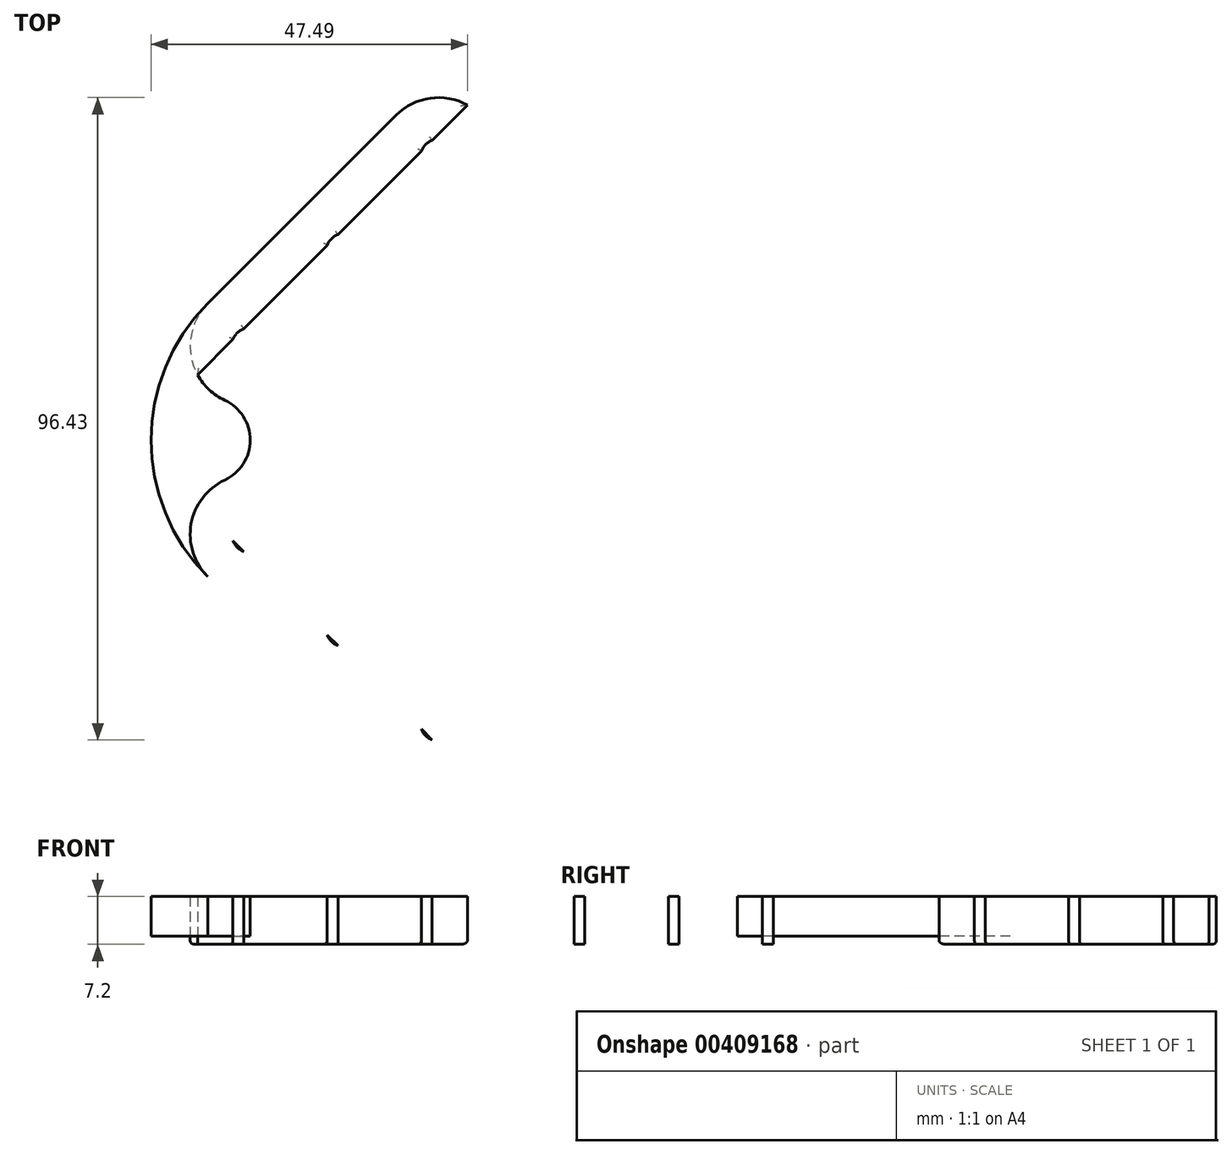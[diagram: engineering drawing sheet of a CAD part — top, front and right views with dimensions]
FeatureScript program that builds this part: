
annotation { "Feature Type Name" : "Feature", "Feature Type Description" : "" }
export const myFeature = defineFeature(function(context is Context, id is Id, definition is map)
    precondition{}
    {
        {
            var Q0;
            Q0=qCreatedBy(makeId("Top.planeOp"),FACE);
            var sketch = newSketch(context, id + "F0", { "sketchPlane" : qUnion([Q0])});
            skLineSegment(sketch, "E0", {"start": v(0, 0) * mm, "end": v(55.95, 55.95) * mm, "construction": true});
            skLineSegment(sketch, "E1", {"start": v(55.95, -55.95) * mm, "end": v(0, 0) * mm, "construction": true});
            skLineSegment(sketch, "E2", {"start": v(0, 14.14) * mm, "end": v(14.14, 0) * mm});
            skLineSegment(sketch, "E3", {"start": v(14.14, 0) * mm, "end": v(0, -14.14) * mm});
            skCircle(sketch, "E4", {"center": v(14.14, 14.14) * mm, "radius": 10 * mm, "construction": true});
            skCircle(sketch, "E5", {"center": v(14.14, 14.14) * mm, "radius": 2.75 * mm});
            skCircle(sketch, "E6", {"center": v(28.28, 28.28) * mm, "radius": 2.75 * mm});
            skCircle(sketch, "E7", {"center": v(42.43, 42.43) * mm, "radius": 2.75 * mm});
            skArc(sketch, "E8", {"start": v(7.78, 20.5) * mm, "mid": v(5.28, 12.58) * mm, "end": v(10.33, 5.99) * mm});
            skArc(sketch, "E9", {"start": v(48.8, 36.06) * mm, "mid": v(48.8, 48.8) * mm, "end": v(36.06, 48.8) * mm});
            skLineSegment(sketch, "E10", {"start": v(7.78, 20.5) * mm, "end": v(36.06, 48.8) * mm});
            skLineSegment(sketch, "E11", {"start": v(23.59, 10.86) * mm, "end": v(20.5, 7.78) * mm, "construction": true});
            skCircle(sketch, "E12.MirrorC", {"center": v(14.14, -14.14) * mm, "radius": 2.75 * mm});
            skLineSegment(sketch, "E13.MirrorCS", {"start": v(0, -14.14) * mm, "end": v(14.14, 0) * mm, "construction": true});
            skCircle(sketch, "E14.MirrorC", {"center": v(28.28, -28.28) * mm, "radius": 2.75 * mm});
            skCircle(sketch, "E15.MirrorC", {"center": v(42.43, -42.43) * mm, "radius": 2.75 * mm});
            skArc(sketch, "E16.MirrorCS", {"start": v(7.78, -20.5) * mm, "mid": v(5.28, -12.58) * mm, "end": v(10.33, -5.99) * mm});
            skLineSegment(sketch, "E17.MirrorCS", {"start": v(0, 0) * mm, "end": v(55.95, -55.95) * mm, "construction": true});
            skCircle(sketch, "E18.MirrorC", {"center": v(14.14, -14.14) * mm, "radius": 10 * mm, "construction": true});
            skArc(sketch, "E19.MirrorCS", {"start": v(48.8, -36.06) * mm, "mid": v(48.8, -48.8) * mm, "end": v(36.06, -48.8) * mm});
            skLineSegment(sketch, "E20.MirrorCS", {"start": v(7.78, -20.5) * mm, "end": v(36.06, -48.8) * mm});
            skArc(sketch, "E21", {"start": v(10.33, 5.99) * mm, "mid": v(14.14, 0) * mm, "end": v(10.33, -5.99) * mm});
            skArc(sketch, "E22", {"start": v(48.8, 36.06) * mm, "mid": v(33.85, 0) * mm, "end": v(48.8, -36.06) * mm});
            skCircle(sketch, "E23", {"center": v(28.28, 28.28) * mm, "radius": 2.5 * mm, "construction": true});
            skLineSegment(sketch, "E24", {"start": v(50.3, 46.77) * mm, "end": v(9.8, 6.26) * mm});
            skLineSegment(sketch, "E25.MirrorCS", {"start": v(46.77, 50.3) * mm, "end": v(6.26, 9.8) * mm});
            skLineSegment(sketch, "E26.MirrorCS", {"start": v(46.77, -50.3) * mm, "end": v(6.26, -9.8) * mm});
            skLineSegment(sketch, "E27.MirrorCS", {"start": v(50.3, -46.77) * mm, "end": v(9.8, -6.26) * mm});
            skArc(sketch, "E28", {"start": v(7.78, 20.5) * mm, "mid": v(-0.72, 0) * mm, "end": v(7.78, -20.5) * mm});
            skSolve(sketch);
        }
        {
            var Q0;
            {var subQ4=sQuery(id+"F0.wireOp",EDGE,"E21");Q0=makeQuery(id+"F0.imprint","IMPRINT",FACE,{"disambiguationData":[TD([[makeQuery(id+"F0.imprint","IMPRINT",EDGE,{"derivedFrom":subQ4}),1.0]])]});}
            var Q1;
            {var subQ0=sQuery(id+"F0.wireOp",EDGE,"E10");Q1=makeQuery(id+"F0.imprint","IMPRINT",FACE,{"disambiguationData":[TD([[makeQuery(id+"F0.imprint","IMPRINT",EDGE,{"derivedFrom":subQ0}),-1.0]])]});}
            var Q2;
            {var subQ0=sQuery(id+"F0.wireOp",EDGE,"E25.MirrorCS");var subQ1=sQuery(id+"F0.wireOp",EDGE,"E6");var subQ2=makeQuery(id+"F0.imprint","INTERSECT",VERTEX,{"disambiguationData":[OD(1.0)],"derivedFrom":[subQ1,subQ0]});Q2=makeQuery(id+"F0.imprint","IMPRINT",FACE,{"disambiguationData":[TD([[makeQuery(id+"F0.imprint","IMPRINT",EDGE,{"disambiguationData":[TD([[subQ2,1.0]])],"derivedFrom":subQ1}),-1.0]])]});}
            var Q3;
            {var subQ0=sQuery(id+"F0.wireOp",EDGE,"E25.MirrorCS");var subQ1=sQuery(id+"F0.wireOp",EDGE,"E7");var subQ2=makeQuery(id+"F0.imprint","INTERSECT",VERTEX,{"disambiguationData":[OD(1.0)],"derivedFrom":[subQ1,subQ0]});Q3=makeQuery(id+"F0.imprint","IMPRINT",FACE,{"disambiguationData":[TD([[makeQuery(id+"F0.imprint","IMPRINT",EDGE,{"disambiguationData":[TD([[subQ2,1.0]])],"derivedFrom":subQ1}),-1.0]])]});}
            var Q4;
            {var subQ0=sQuery(id+"F0.wireOp",EDGE,"E25.MirrorCS");var subQ1=sQuery(id+"F0.wireOp",EDGE,"E5");var subQ2=makeQuery(id+"F0.imprint","INTERSECT",VERTEX,{"disambiguationData":[OD(1.0)],"derivedFrom":[subQ1,subQ0]});Q4=makeQuery(id+"F0.imprint","IMPRINT",FACE,{"disambiguationData":[TD([[makeQuery(id+"F0.imprint","IMPRINT",EDGE,{"disambiguationData":[TD([[subQ2,1.0]])],"derivedFrom":subQ1}),-1.0]])]});}
            var Q5;
            {var subQ0=sQuery(id+"F0.wireOp",EDGE,"E25.MirrorCS");var subQ1=sQuery(id+"F0.wireOp",EDGE,"E5");var subQ2=makeQuery(id+"F0.imprint","INTERSECT",VERTEX,{"disambiguationData":[OD(0.0)],"derivedFrom":[subQ1,subQ0]});Q5=makeQuery(id+"F0.imprint","IMPRINT",FACE,{"disambiguationData":[TD([[makeQuery(id+"F0.imprint","IMPRINT",EDGE,{"disambiguationData":[TD([[subQ2,-1.0]])],"derivedFrom":subQ1}),-1.0]])]});}
            var Q6;
            {var subQ0=sQuery(id+"F0.wireOp",EDGE,"E26.MirrorCS");var subQ1=sQuery(id+"F0.wireOp",EDGE,"E12.MirrorC");var subQ2=makeQuery(id+"F0.imprint","INTERSECT",VERTEX,{"disambiguationData":[OD(0.0)],"derivedFrom":[subQ1,subQ0]});Q6=makeQuery(id+"F0.imprint","IMPRINT",FACE,{"disambiguationData":[TD([[makeQuery(id+"F0.imprint","IMPRINT",EDGE,{"disambiguationData":[TD([[subQ2,-1.0]])],"derivedFrom":subQ1}),1.0]])]});}
            var Q7;
            {var subQ0=sQuery(id+"F0.wireOp",EDGE,"E26.MirrorCS");var subQ1=sQuery(id+"F0.wireOp",EDGE,"E12.MirrorC");var subQ2=makeQuery(id+"F0.imprint","INTERSECT",VERTEX,{"disambiguationData":[OD(1.0)],"derivedFrom":[subQ1,subQ0]});Q7=makeQuery(id+"F0.imprint","IMPRINT",FACE,{"disambiguationData":[TD([[makeQuery(id+"F0.imprint","IMPRINT",EDGE,{"disambiguationData":[TD([[subQ2,1.0]])],"derivedFrom":subQ1}),1.0]])]});}
            var Q8;
            {var subQ0=sQuery(id+"F0.wireOp",EDGE,"E26.MirrorCS");var subQ1=sQuery(id+"F0.wireOp",EDGE,"E14.MirrorC");var subQ2=makeQuery(id+"F0.imprint","INTERSECT",VERTEX,{"disambiguationData":[OD(1.0)],"derivedFrom":[subQ1,subQ0]});Q8=makeQuery(id+"F0.imprint","IMPRINT",FACE,{"disambiguationData":[TD([[makeQuery(id+"F0.imprint","IMPRINT",EDGE,{"disambiguationData":[TD([[subQ2,1.0]])],"derivedFrom":subQ1}),1.0]])]});}
            var Q9;
            {var subQ0=sQuery(id+"F0.wireOp",EDGE,"E26.MirrorCS");var subQ1=sQuery(id+"F0.wireOp",EDGE,"E15.MirrorC");var subQ2=makeQuery(id+"F0.imprint","INTERSECT",VERTEX,{"disambiguationData":[OD(1.0)],"derivedFrom":[subQ1,subQ0]});Q9=makeQuery(id+"F0.imprint","IMPRINT",FACE,{"disambiguationData":[TD([[makeQuery(id+"F0.imprint","IMPRINT",EDGE,{"disambiguationData":[TD([[subQ2,1.0]])],"derivedFrom":subQ1}),1.0]])]});}
            var Q10;
            {var subQ0=sQuery(id+"F0.wireOp",EDGE,"E20.MirrorCS");Q10=makeQuery(id+"F0.imprint","IMPRINT",FACE,{"disambiguationData":[TD([[makeQuery(id+"F0.imprint","IMPRINT",EDGE,{"derivedFrom":subQ0}),1.0]])]});}
            var Q11;
            {var subQ3=sQuery(id+"F0.wireOp",EDGE,"E21");Q11=makeQuery(id+"F0.imprint","IMPRINT",FACE,{"disambiguationData":[TD([[makeQuery(id+"F0.imprint","IMPRINT",EDGE,{"derivedFrom":subQ3}),-1.0]])]});}
            var Q12;
            {var subQ1=sQuery(id+"F0.wireOp",EDGE,"E2");var subQ3=sQuery(id+"F0.wireOp",EDGE,"E28");var subQ4=makeQuery(id+"F0.imprint","INTERSECT",VERTEX,{"derivedFrom":[subQ1,subQ3]});Q12=makeQuery(id+"F0.imprint","IMPRINT",FACE,{"disambiguationData":[TD([[makeQuery(id+"F0.imprint","IMPRINT",EDGE,{"disambiguationData":[TD([[subQ4,-1.0]])],"derivedFrom":subQ3}),1.0]])]});}
            extrude(context, id + "F1", {"entities" : qUnion([Q0, Q1, Q2, Q3, Q4, Q5, Q6, Q7, Q8, Q9, Q10, Q11, Q12]), "depth" : 6 * mm, "offsetDistance" : 25 * mm});
        }
        {
            var Q0;
            {var subQ0=sQuery(id+"F0.wireOp",EDGE,"E25.MirrorCS");var subQ1=sQuery(id+"F0.wireOp",EDGE,"E7");var subQ2=makeQuery(id+"F0.imprint","INTERSECT",VERTEX,{"disambiguationData":[OD(1.0)],"derivedFrom":[subQ1,subQ0]});Q0=makeQuery(id+"F0.imprint","IMPRINT",FACE,{"disambiguationData":[TD([[makeQuery(id+"F0.imprint","IMPRINT",EDGE,{"disambiguationData":[TD([[subQ2,1.0]])],"derivedFrom":subQ1}),-1.0]])]});}
            var Q1;
            {var subQ0=sQuery(id+"F0.wireOp",EDGE,"E25.MirrorCS");var subQ1=sQuery(id+"F0.wireOp",EDGE,"E6");var subQ2=makeQuery(id+"F0.imprint","INTERSECT",VERTEX,{"disambiguationData":[OD(1.0)],"derivedFrom":[subQ1,subQ0]});Q1=makeQuery(id+"F0.imprint","IMPRINT",FACE,{"disambiguationData":[TD([[makeQuery(id+"F0.imprint","IMPRINT",EDGE,{"disambiguationData":[TD([[subQ2,1.0]])],"derivedFrom":subQ1}),-1.0]])]});}
            var Q2;
            {var subQ0=sQuery(id+"F0.wireOp",EDGE,"E25.MirrorCS");var subQ1=sQuery(id+"F0.wireOp",EDGE,"E5");var subQ2=makeQuery(id+"F0.imprint","INTERSECT",VERTEX,{"disambiguationData":[OD(1.0)],"derivedFrom":[subQ1,subQ0]});Q2=makeQuery(id+"F0.imprint","IMPRINT",FACE,{"disambiguationData":[TD([[makeQuery(id+"F0.imprint","IMPRINT",EDGE,{"disambiguationData":[TD([[subQ2,1.0]])],"derivedFrom":subQ1}),-1.0]])]});}
            var Q3;
            {var subQ0=sQuery(id+"F0.wireOp",EDGE,"E25.MirrorCS");var subQ1=sQuery(id+"F0.wireOp",EDGE,"E5");var subQ2=makeQuery(id+"F0.imprint","INTERSECT",VERTEX,{"disambiguationData":[OD(0.0)],"derivedFrom":[subQ1,subQ0]});Q3=makeQuery(id+"F0.imprint","IMPRINT",FACE,{"disambiguationData":[TD([[makeQuery(id+"F0.imprint","IMPRINT",EDGE,{"disambiguationData":[TD([[subQ2,-1.0]])],"derivedFrom":subQ1}),-1.0]])]});}
            var Q4;
            {var subQ0=sQuery(id+"F0.wireOp",EDGE,"E26.MirrorCS");var subQ1=sQuery(id+"F0.wireOp",EDGE,"E12.MirrorC");var subQ2=makeQuery(id+"F0.imprint","INTERSECT",VERTEX,{"disambiguationData":[OD(0.0)],"derivedFrom":[subQ1,subQ0]});Q4=makeQuery(id+"F0.imprint","IMPRINT",FACE,{"disambiguationData":[TD([[makeQuery(id+"F0.imprint","IMPRINT",EDGE,{"disambiguationData":[TD([[subQ2,-1.0]])],"derivedFrom":subQ1}),1.0]])]});}
            var Q5;
            {var subQ0=sQuery(id+"F0.wireOp",EDGE,"E26.MirrorCS");var subQ1=sQuery(id+"F0.wireOp",EDGE,"E12.MirrorC");var subQ2=makeQuery(id+"F0.imprint","INTERSECT",VERTEX,{"disambiguationData":[OD(1.0)],"derivedFrom":[subQ1,subQ0]});Q5=makeQuery(id+"F0.imprint","IMPRINT",FACE,{"disambiguationData":[TD([[makeQuery(id+"F0.imprint","IMPRINT",EDGE,{"disambiguationData":[TD([[subQ2,1.0]])],"derivedFrom":subQ1}),1.0]])]});}
            var Q6;
            {var subQ0=sQuery(id+"F0.wireOp",EDGE,"E26.MirrorCS");var subQ1=sQuery(id+"F0.wireOp",EDGE,"E14.MirrorC");var subQ2=makeQuery(id+"F0.imprint","INTERSECT",VERTEX,{"disambiguationData":[OD(1.0)],"derivedFrom":[subQ1,subQ0]});Q6=makeQuery(id+"F0.imprint","IMPRINT",FACE,{"disambiguationData":[TD([[makeQuery(id+"F0.imprint","IMPRINT",EDGE,{"disambiguationData":[TD([[subQ2,1.0]])],"derivedFrom":subQ1}),1.0]])]});}
            var Q7;
            {var subQ0=sQuery(id+"F0.wireOp",EDGE,"E26.MirrorCS");var subQ1=sQuery(id+"F0.wireOp",EDGE,"E15.MirrorC");var subQ2=makeQuery(id+"F0.imprint","INTERSECT",VERTEX,{"disambiguationData":[OD(1.0)],"derivedFrom":[subQ1,subQ0]});Q7=makeQuery(id+"F0.imprint","IMPRINT",FACE,{"disambiguationData":[TD([[makeQuery(id+"F0.imprint","IMPRINT",EDGE,{"disambiguationData":[TD([[subQ2,1.0]])],"derivedFrom":subQ1}),1.0]])]});}
            extrude(context, id + "F2", {"entities" : qUnion([Q0, Q1, Q2, Q3, Q4, Q5, Q6, Q7]), "operationType" : NewBodyOperationType.ADD, "oppositeDirection" : true, "depth" : 1.2 * mm, "offsetDistance" : 25 * mm});
        }
        {
            var Q0;
            Q0=makeQuery(id+"F2.opExtrude","CAP_FACE",FACE,{"disambiguationData":[OSD([sQuery(id+"F0.wireOp",EDGE,"E6"),sQuery(id+"F0.wireOp",EDGE,"E7"),sQuery(id+"F0.wireOp",EDGE,"E24"),sQuery(id+"F0.wireOp",EDGE,"E25.MirrorCS")])],"isStart":false});
            var Q1;
            Q1=makeQuery(id+"F2.opExtrude","CAP_FACE",FACE,{"disambiguationData":[OSD([sQuery(id+"F0.wireOp",EDGE,"E7"),sQuery(id+"F0.wireOp",EDGE,"E9"),sQuery(id+"F0.wireOp",EDGE,"E24"),sQuery(id+"F0.wireOp",EDGE,"E25.MirrorCS")])],"isStart":false});
            var Q2;
            Q2=makeQuery(id+"F2.opExtrude","CAP_FACE",FACE,{"disambiguationData":[OSD([sQuery(id+"F0.wireOp",EDGE,"E5"),sQuery(id+"F0.wireOp",EDGE,"E6"),sQuery(id+"F0.wireOp",EDGE,"E24"),sQuery(id+"F0.wireOp",EDGE,"E25.MirrorCS")])],"isStart":false});
            var Q3;
            Q3=makeQuery(id+"F2.opExtrude","CAP_FACE",FACE,{"disambiguationData":[OSD([sQuery(id+"F0.wireOp",EDGE,"E5"),sQuery(id+"F0.wireOp",EDGE,"E8"),sQuery(id+"F0.wireOp",EDGE,"E24"),sQuery(id+"F0.wireOp",EDGE,"E25.MirrorCS")])],"isStart":false});
            var Q4;
            Q4=makeQuery(id+"F2.opExtrude","CAP_FACE",FACE,{"disambiguationData":[OSD([sQuery(id+"F0.wireOp",EDGE,"E12.MirrorC"),sQuery(id+"F0.wireOp",EDGE,"E16.MirrorCS"),sQuery(id+"F0.wireOp",EDGE,"E26.MirrorCS"),sQuery(id+"F0.wireOp",EDGE,"E27.MirrorCS")])],"isStart":false});
            var Q5;
            Q5=makeQuery(id+"F2.opExtrude","CAP_FACE",FACE,{"disambiguationData":[OSD([sQuery(id+"F0.wireOp",EDGE,"E12.MirrorC"),sQuery(id+"F0.wireOp",EDGE,"E14.MirrorC"),sQuery(id+"F0.wireOp",EDGE,"E26.MirrorCS"),sQuery(id+"F0.wireOp",EDGE,"E27.MirrorCS")])],"isStart":false});
            var Q6;
            Q6=makeQuery(id+"F2.opExtrude","CAP_FACE",FACE,{"disambiguationData":[OSD([sQuery(id+"F0.wireOp",EDGE,"E15.MirrorC"),sQuery(id+"F0.wireOp",EDGE,"E19.MirrorCS"),sQuery(id+"F0.wireOp",EDGE,"E26.MirrorCS"),sQuery(id+"F0.wireOp",EDGE,"E27.MirrorCS")])],"isStart":false});
            var Q7;
            Q7=makeQuery(id+"F2.opExtrude","CAP_FACE",FACE,{"disambiguationData":[OSD([sQuery(id+"F0.wireOp",EDGE,"E14.MirrorC"),sQuery(id+"F0.wireOp",EDGE,"E15.MirrorC"),sQuery(id+"F0.wireOp",EDGE,"E26.MirrorCS"),sQuery(id+"F0.wireOp",EDGE,"E27.MirrorCS")])],"isStart":false});
            var Q8;
            Q8=makeQuery(id+"F2.opExtrude","CAP_FACE",FACE,{"disambiguationData":[OSD([sQuery(id+"F0.wireOp",EDGE,"E2"),sQuery(id+"F0.wireOp",EDGE,"E3"),sQuery(id+"F0.wireOp",EDGE,"E28")])],"isStart":false});
            fillet(context, id + "F3", {"entities" : qUnion([Q0, Q1, Q2, Q3, Q4, Q5, Q6, Q7, Q8]), "radius" : 0.6 * mm, "tangentPropagation" : true, "allowEdgeOverflow" : false});
        }
    });
